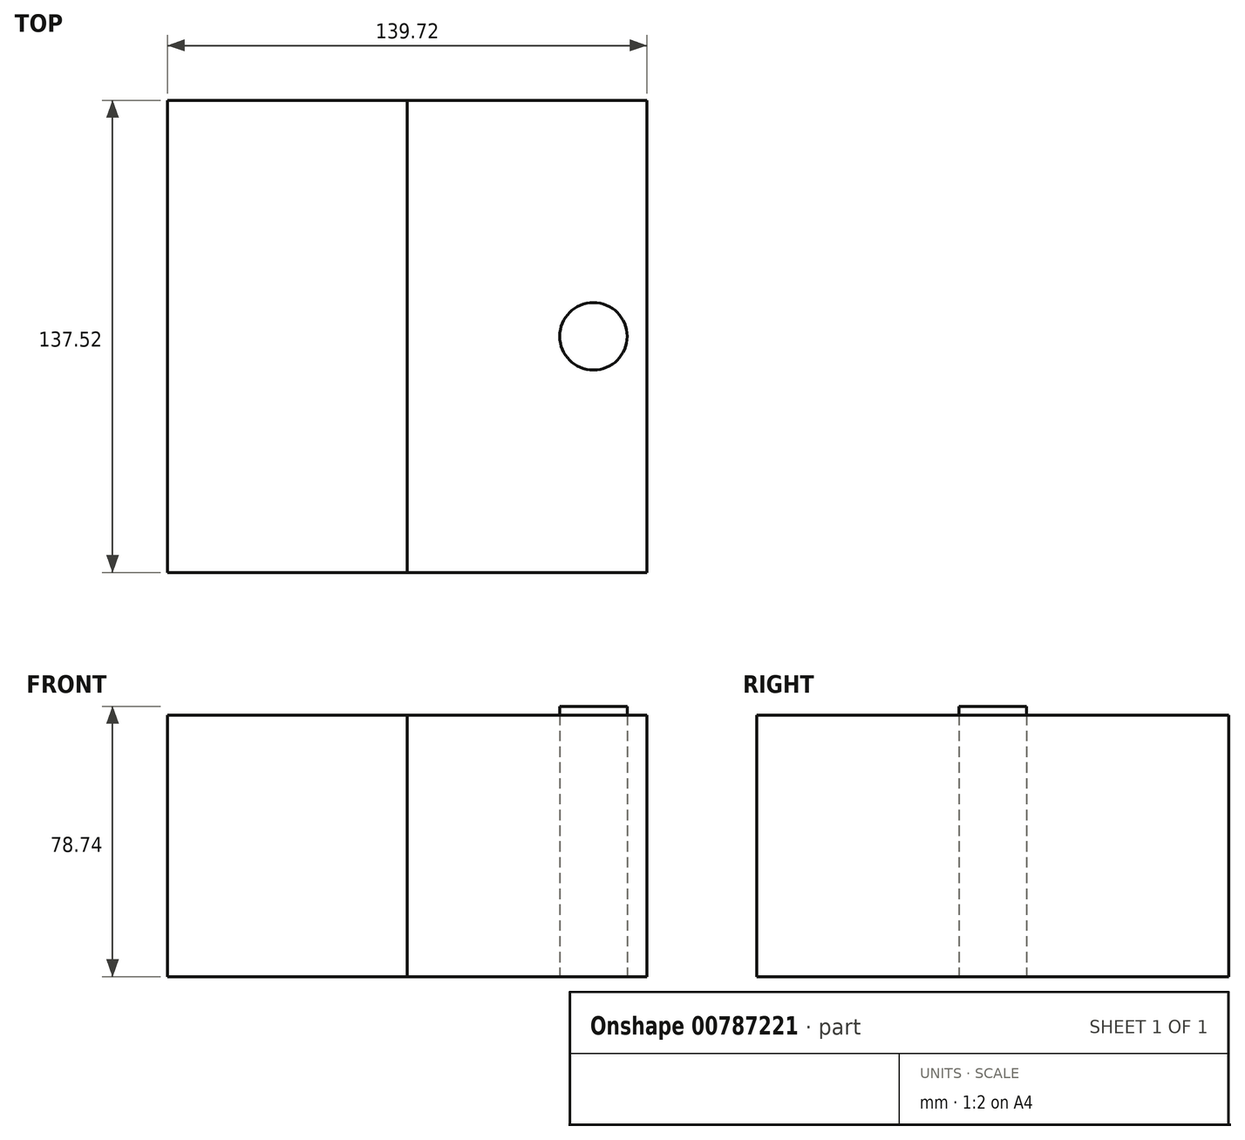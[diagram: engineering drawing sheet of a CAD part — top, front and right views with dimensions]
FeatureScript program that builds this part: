
annotation { "Feature Type Name" : "Feature", "Feature Type Description" : "" }
export const myFeature = defineFeature(function(context is Context, id is Id, definition is map)
    precondition{}
    {
        {
            var Q0;
            Q0=qCreatedBy(makeId("Top.planeOp"),FACE);
            var sketch = newSketch(context, id + "F0", { "sketchPlane" : qUnion([Q0])});
            skLineSegment(sketch, "E0.bottom", {"start": v(69.86, -68.76) * mm, "end": v(-69.86, -68.76) * mm});
            skLineSegment(sketch, "E0.top", {"start": v(69.86, 68.76) * mm, "end": v(-69.86, 68.76) * mm});
            skLineSegment(sketch, "E0.left", {"start": v(69.86, -68.76) * mm, "end": v(69.86, 68.76) * mm});
            skLineSegment(sketch, "E0.right", {"start": v(-69.86, -68.76) * mm, "end": v(-69.86, 68.76) * mm});
            skPoint(sketch, "E0.middle", {"position": v(0, 0) * mm});
            skLineSegment(sketch, "E1", {"start": v(0, 68.76) * mm, "end": v(0, -68.76) * mm});
            skSolve(sketch);
        }
        {
            var Q0;
            Q0=qCreatedBy(makeId("Top.planeOp"),FACE);
            var sketch = newSketch(context, id + "F1", { "sketchPlane" : qUnion([Q0])});
            skCircle(sketch, "E2", {"center": v(54.26, 0) * mm, "radius": 9.82 * mm});
            skSolve(sketch);
        }
        {
            var Q0;
            {var subQ0=sQuery(id+"F0.wireOp",EDGE,"E0.right");Q0=makeQuery(id+"F0.imprint","IMPRINT",FACE,{"disambiguationData":[TD([[makeQuery(id+"F0.imprint","IMPRINT",EDGE,{"derivedFrom":subQ0}),-1.0]])]});}
            extrude(context, id + "F2", {"entities" : qUnion([Q0]), "depth" : 76.2 * mm, "offsetDistance" : 25.4 * mm});
        }
        {
            var Q0;
            Q0=makeQuery(id+"F1.imprint","IMPRINT",FACE,{"disambiguationData":[TD([[makeQuery(id+"F1.imprint","IMPRINT",EDGE,{"derivedFrom":sQuery(id+"F1.wireOp",EDGE,"E2")}),1.0]])]});
            extrude(context, id + "F3", {"entities" : qUnion([Q0]), "depth" : 78.74 * mm, "offsetDistance" : 25.4 * mm});
        }
        {
            var Q0;
            {var subQ0=sQuery(id+"F0.wireOp",EDGE,"E0.left");Q0=makeQuery(id+"F0.imprint","IMPRINT",FACE,{"disambiguationData":[TD([[makeQuery(id+"F0.imprint","IMPRINT",EDGE,{"derivedFrom":subQ0}),1.0]])]});}
            extrude(context, id + "F4", {"entities" : qUnion([Q0]), "depth" : 76.2 * mm, "offsetDistance" : 25.4 * mm});
        }
    });
